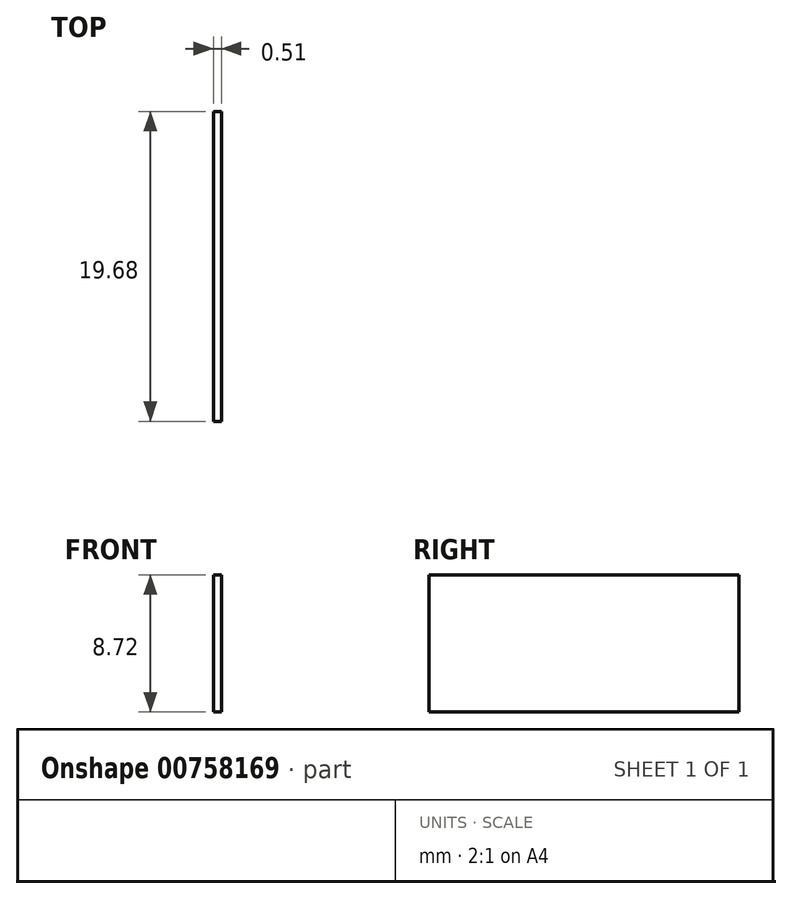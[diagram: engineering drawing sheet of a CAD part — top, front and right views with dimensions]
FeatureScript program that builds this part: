
annotation { "Feature Type Name" : "Feature", "Feature Type Description" : "" }
export const myFeature = defineFeature(function(context is Context, id is Id, definition is map)
    precondition{}
    {
        {
            var Q0;
            Q0=qCreatedBy(makeId("Right.planeOp"),FACE);
            var sketch = newSketch(context, id + "F0", { "sketchPlane" : qUnion([Q0])});
            skLineSegment(sketch, "E0.bottom", {"start": v(-36.63, 47.77) * mm, "end": v(-16.95, 47.77) * mm});
            skLineSegment(sketch, "E0.top", {"start": v(-36.63, 39.05) * mm, "end": v(-16.95, 39.05) * mm});
            skLineSegment(sketch, "E0.left", {"start": v(-36.63, 47.77) * mm, "end": v(-36.63, 39.05) * mm});
            skLineSegment(sketch, "E0.right", {"start": v(-16.95, 47.77) * mm, "end": v(-16.95, 39.05) * mm});
            skSolve(sketch);
        }
        {
            var Q0;
            Q0 = qSketchRegion(id + "F0", true);
            extrude(context, id + "F1", {"entities" : qUnion([Q0]), "depth" : 0.5 * mm, "offsetDistance" : 25.4 * mm});
        }
    });
